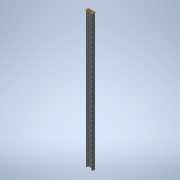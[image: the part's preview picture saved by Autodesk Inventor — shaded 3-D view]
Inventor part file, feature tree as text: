
AUTODESK INVENTOR PART (.ipt)
format: ipt  version: 2020 (Build 240168000, 168)  size: 479,744 bytes
history: native  units: in
note: dims shown in document units (in); Inventor stores cm internally (conversion verified against a paired STEP export)
features: other x36, boolean_combine x1, extrude x1, pattern_linear x1, plane x1, split x1, imported_body x1, sketch x1
ambient origin geometry x8: Origin, YZ Plane, XZ Plane, XY Plane, X Axis, Y Axis, Z Axis, Center Point
bodies: Body1 (feature_tree)
feature tree (43):
  boolean_combine  "Combine1"
  other  "Linear Slide"
  other  "Work Axis1"
  extrude  "Extrusion1"  TaperAngle=0.0deg  [1 undecoded]
  pattern_linear  "Rectangular Pattern1"  Spacing1=0.0in  [1 undecoded]
  other  "bottom plane"
  other  "top plane"
  plane  "Work Plane3"
  split  "Split1"
  imported_body  "Base1"
  other  "Work Point1"
  other  "Work Axis2"
  sketch  "Sketch1"  dims[d0=12.5984in d2=0.5in d4=0.0in d5=0.0in d6=0.0in d8=0.0in]
  other  "Work Axis46"
  other  "Work Axis47"
  other  "Work Axis48"
  other  "Work Axis49"
  other  "Work Axis50"
  other  "Work Axis51"
  other  "Work Axis52"
  other  "Work Axis53"
  other  "Work Axis54"
  other  "Work Axis55"
  other  "Work Axis56"
  other  "Work Axis57"
  other  "Work Axis69"
  other  "Work Axis70"
  other  "Work Axis71"
  other  "Work Axis72"
  other  "Work Axis73"
  other  "Work Axis74"
  other  "Work Axis75"
  other  "Work Axis76"
  other  "Work Axis77"
  other  "Work Axis78"
  other  "Work Axis90"
  other  "Work Axis91"
  other  "Work Axis92"
  other  "Work Axis93"
  other  "Work Axis94"
  other  "Work Axis95"
  other  "Work Axis96"
  other  "Work Axis97"
note: 2 required parameter values undecoded (feature->parameter linkage not recoverable at this tier; creation-order binding heuristic only, values carry confidence <= 0.55)
